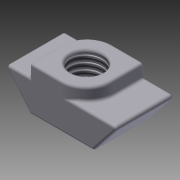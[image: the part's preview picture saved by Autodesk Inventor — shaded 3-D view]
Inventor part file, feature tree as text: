
AUTODESK INVENTOR PART (.ipt)
format: ipt  version: 2011 (Build 150239000, 239)  size: 195,072 bytes
history: native  units: in
note: dims shown in document units (in); Inventor stores cm internally (conversion verified against a paired STEP export)
features: extrude x2, fillet x2, sketch x2, thread x1
ambient origin geometry x8: Origin, YZ Plane, XZ Plane, XY Plane, X Axis, Y Axis, Z Axis, Center Point
bodies: Solid1 (feature_tree)
feature tree (7):
  extrude  "Extrusion1"  Depth=0.225in
  extrude  "Extrusion2"  Depth=0.25in
  fillet  "Fillet1"  Radius=0.1in
  fillet  "Fillet2"  Radius=0.05in
  thread  "Thread1"  [1 undecoded]
  sketch  "Sketch1"  dims[d0=0.45in d1=0.225in]
  sketch  "Sketch2"  dims[d2=0.125in d3=0.25in d4=0.1in d5=0.05in d6=0.1in d7=0.225in d8=0.0in d9=0.125in d10=1.0in d11=0.0in d12=0.1in d13=0.01in d14=1.0in d15=0.0in]
note: 1 required parameter value undecoded (feature->parameter linkage not recoverable at this tier; creation-order binding heuristic only, values carry confidence <= 0.55)
